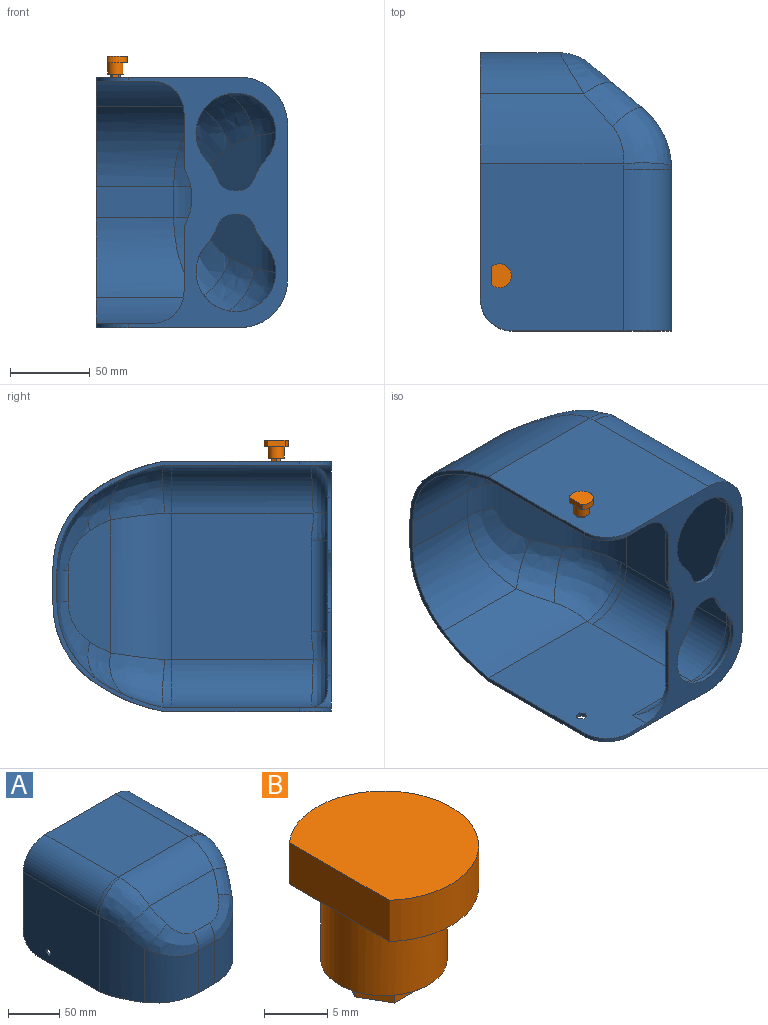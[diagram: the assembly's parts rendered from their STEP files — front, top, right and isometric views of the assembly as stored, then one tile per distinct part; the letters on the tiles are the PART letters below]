
ASSEMBLY  parts=2 mates=1
PART A: 87 faces, bbox 158.6x174.5x120.3 mm
  f0: cylinder r=110.63mm len=87.5mm, axis (0,0,-1), area 3450.1mm2, adj f5,f10,f17,f57,f58,f59
  f1: cylinder r=110.63mm len=87.5mm, axis (0,0,-1), area 3450.1mm2, adj f6,f9,f17,f64,f65,f66
  f2: plane 83.39x31.77mm, normal (0,0.77,-0.64), area 2722mm2, adj f54,f59,f60,f61,f62,f64
  f3: plane 157x100mm, normal (0,1,0), area 5587mm2, adj f4,f5,f6,f11,f15,f16,f21,f23
  f4: plane 33.64x2.5mm, normal (0,0,-1), area 84.1mm2, adj f3,f22,f25,f26
  f5: plane 104.74x87.5mm, normal (1,0,0), area 8392.5mm2, adj f0,f3,f17,f24,f40,f48,f49,f50
  f6: plane 104.74x87.5mm, normal (-1,0,0), area 8392.5mm2, adj f1,f3,f17,f25,f41,f42,f43,f44
  f7: plane 92.01x88.86mm, normal (0,0,-1), area 8078.7mm2, adj f54,f56,f63,f81,f82,f83
  f8: plane 48.58x19.33mm, normal (0,1,0), area 939.2mm2, adj f9,f10,f17,f61
  f9: cylinder r=60mm len=64.79mm, axis (0,0,-1), area 3375.4mm2, adj f1,f8,f17,f62
  f10: cylinder r=60mm len=64.79mm, axis (0,0,-1), area 3375.4mm2, adj f0,f8,f17,f60
  f11: plane 104.97x90mm, normal (-1,0,0), area 9330mm2, adj f3,f12,f17,f40,f48,f49,f50,f51
  f12: cylinder r=113.13mm len=90mm, axis (0,0,-1), area 3852.8mm2, adj f11,f17,f19,f68,f69,f70
  f13: plane 49.49x22mm, normal (0,-1,0), area 1088.6mm2, adj f17,f18,f19,f72
  f14: cylinder r=113.13mm len=90mm, axis (0,0,-1), area 3852.8mm2, adj f15,f17,f18,f75,f76,f77
  f15: plane 104.97x90mm, normal (1,0,0), area 9330mm2, adj f3,f14,f17,f41,f42,f43,f44,f45
  f16: plane 101.18x97mm, normal (0,0,1), area 9814.9mm2, adj f3,f55,f67,f73
  f17: plane 157x154.5mm, normal (0,0,-1), area 1023.4mm2, adj f0,f1,f5,f6,f8,f9,f10,f11
  f18: cylinder r=60mm len=64.94mm, axis (0,0,-1), area 3318.7mm2, adj f13,f14,f17,f74
  f19: cylinder r=60mm len=64.94mm, axis (0,0,-1), area 3318.7mm2, adj f12,f13,f17,f71
  f20: plane 87.84x33.36mm, normal (0,-0.77,0.64), area 3020.2mm2, adj f55,f70,f71,f72,f74,f76
  f21: plane 39.64x2.5mm, normal (0,0,-1), area 99.1mm2, adj f3,f22,f24,f27
  f22: plane 132x55.18mm, normal (0,-1,0), area 2589.6mm2, adj f4,f21,f23,f24,f25,f26,f27,f28
  f23: cylinder r=35mm len=33.89mm, axis (0,1,0), area 88.4mm2, adj f3,f22,f26,f27
  f24: cylinder r=20mm len=20mm, axis (0,-1,0), area 157.9mm2, adj f3,f5,f21,f22,f78
  f25: cylinder r=20mm len=20mm, axis (0,1,0), area 157.9mm2, adj f3,f4,f6,f22,f85
  f26: cylinder r=5mm len=2.5mm, axis (0,1,0), area 6.3mm2, adj f3,f4,f22,f23
  f27: cylinder r=5mm len=2.5mm, axis (0,1,0), area 6.3mm2, adj f3,f21,f22,f23
  f28: cylinder r=25mm len=50mm, axis (0,1,0), area 278.5mm2, adj f3,f22,f29,f33,f79,f80,f81
  f29: cylinder r=41.31mm len=14.09mm, axis (0,1,0), area 41.6mm2, adj f3,f22,f28,f30
  f30: cylinder r=10mm len=9.4mm, axis (0,1,0), area 30.6mm2, adj f3,f22,f29,f31
  f31: plane 3.54x2.5mm, normal (-1,0,0), area 8.8mm2, adj f3,f22,f30,f32
  f32: cylinder r=10mm len=9.4mm, axis (0,1,0), area 30.6mm2, adj f3,f22,f31,f33
  f33: cylinder r=41.31mm len=14.09mm, axis (0,1,0), area 41.6mm2, adj f3,f22,f28,f32
  f34: cylinder r=10mm len=9.4mm, axis (0,1,0), area 30.6mm2, adj f3,f22,f35,f39
  f35: cylinder r=41.31mm len=13.04mm, axis (0,1,0), area 38.1mm2, adj f3,f22,f34,f36
  f36: cylinder r=25mm len=50mm, axis (0,1,0), area 285.9mm2, adj f3,f22,f35,f37,f83,f84,f86
  f37: cylinder r=41.31mm len=13.04mm, axis (0,1,0), area 38.1mm2, adj f3,f22,f36,f38
  f38: cylinder r=10mm len=9.4mm, axis (0,1,0), area 30.6mm2, adj f3,f22,f37,f39
  f39: plane 3.54x2.5mm, normal (1,0,0), area 8.8mm2, adj f3,f22,f34,f38
  f40: cylinder r=20mm len=20mm, axis (-1,0,0), area 78.5mm2, adj f3,f5,f11,f17
  f41: cylinder r=20mm len=20mm, axis (1,0,0), area 78.5mm2, adj f3,f6,f15,f17
  f42: plane 3x2.5mm, normal (0,0.5,0.87), area 8.7mm2, adj f6,f15,f43,f47
  f43: plane 3.46x2.5mm, normal (0,1,0), area 8.7mm2, adj f6,f15,f42,f44
  f44: plane 3x2.5mm, normal (0,0.5,-0.87), area 8.7mm2, adj f6,f15,f43,f45
  f45: plane 3x2.5mm, normal (0,-0.5,-0.87), area 8.7mm2, adj f6,f15,f44,f46
  f46: plane 3.46x2.5mm, normal (0,-1,0), area 8.7mm2, adj f6,f15,f45,f47
  f47: plane 3x2.5mm, normal (0,-0.5,0.87), area 8.7mm2, adj f6,f15,f42,f46
  f48: plane 3x2.5mm, normal (0,-0.5,0.87), area 8.7mm2, adj f5,f11,f49,f53
  f49: plane 3.46x2.5mm, normal (0,-1,0), area 8.7mm2, adj f5,f11,f48,f50
  f50: plane 3x2.5mm, normal (0,-0.5,-0.87), area 8.7mm2, adj f5,f11,f49,f51
  f51: plane 3x2.5mm, normal (0,0.5,-0.87), area 8.7mm2, adj f5,f11,f50,f52
  f52: plane 3.46x2.5mm, normal (0,1,0), area 8.7mm2, adj f5,f11,f51,f53
  f53: plane 3x2.5mm, normal (0,0.5,0.87), area 8.7mm2, adj f5,f11,f48,f52
  f54: cylinder r=50mm len=92mm, axis (1,0,0), area 3844.8mm2, adj f2,f7,f57,f58,f65,f66
  f55: cylinder r=50mm len=97mm, axis (1,0,0), area 4041.8mm2, adj f16,f20,f68,f69,f75,f77
  f56: cylinder r=30mm len=88.77mm, axis (0,-1,0), area 4161.2mm2, adj f5,f7,f57,f80
  f57: torus R=20mm, axis (-1,0,0), area 251.9mm2, adj f0,f5,f54,f56,f58
  f58: bspline ~51.33x39.96mm, area 1529.2mm2, adj f0,f54,f57,f59
  f59: bspline ~39.58x37.07mm, area 854.9mm2, adj f0,f2,f58,f60
  f60: bspline ~53.27x38.51mm, area 1263.7mm2, adj f2,f10,f59,f61
  f61: cylinder r=30mm len=19.33mm, axis (1,0,0), area 404.9mm2, adj f2,f8,f60,f62
  f62: bspline ~53.27x38.51mm, area 1263.7mm2, adj f2,f9,f61,f64
  f63: cylinder r=30mm len=88.77mm, axis (0,1,0), area 4161.2mm2, adj f6,f7,f65,f84
  f64: bspline ~39.58x37.07mm, area 854.9mm2, adj f1,f2,f62,f66
  f65: torus R=20mm, axis (-1,0,0), area 251.9mm2, adj f1,f6,f54,f63,f66
  f66: bspline ~51.33x39.96mm, area 1529.2mm2, adj f1,f54,f64,f65
  f67: cylinder r=30mm len=101.18mm, axis (0,1,0), area 4768.2mm2, adj f3,f11,f16,f68
  f68: torus R=20mm, axis (-1,0,0), area 168.1mm2, adj f11,f12,f55,f67,f69
  f69: bspline ~51.33x39.92mm, area 1615mm2, adj f12,f55,f68,f70
  f70: bspline ~45.39x40.62mm, area 977.5mm2, adj f12,f20,f69,f71
  f71: bspline ~53.27x38.51mm, area 1216.6mm2, adj f19,f20,f70,f72
  f72: cylinder r=30mm len=22mm, axis (-1,0,0), area 460.7mm2, adj f13,f20,f71,f74
  f73: cylinder r=30mm len=101.18mm, axis (0,-1,0), area 4768.2mm2, adj f3,f15,f16,f75
  f74: bspline ~53.27x38.51mm, area 1216.6mm2, adj f18,f20,f72,f76
  f75: torus R=20mm, axis (-1,0,0), area 168.1mm2, adj f14,f15,f55,f73,f77
  f76: bspline ~45.39x40.62mm, area 977.5mm2, adj f14,f20,f74,f77
  f77: bspline ~51.33x39.92mm, area 1615mm2, adj f14,f55,f75,f76
  f78: cylinder r=10mm len=41.6mm, axis (0,0,1), area 517.5mm2, adj f5,f22,f24,f79
  f79: bspline ~14.27x10.62mm, area 152.7mm2, adj f5,f28,f78,f80
  f80: bspline ~34.3x31.74mm, area 530.2mm2, adj f28,f56,f79,f81
  f81: bspline ~23.68x11.42mm, area 213.6mm2, adj f7,f28,f80,f82
  f82: cylinder r=10mm len=57mm, axis (1,0,0), area 895.4mm2, adj f7,f22,f81,f83
  f83: bspline ~23.68x11.42mm, area 213.6mm2, adj f7,f36,f82,f84
  f84: bspline ~30x30mm, area 530.2mm2, adj f36,f63,f83,f86
  f85: cylinder r=10mm len=41.6mm, axis (0,0,-1), area 517.5mm2, adj f6,f22,f25,f86
  f86: bspline ~14.27x10.62mm, area 152.7mm2, adj f6,f36,f84,f85
PART B: 16 faces, bbox 12.5x15x13 mm
  f0: cylinder r=7.5mm len=15mm, axis (0,0,-1), area 138mm2, adj f1,f2,f12
  f1: plane 15x12.5mm, normal (0,0,1), area 157.4mm2, adj f0,f12
  f2: plane 15x12.5mm, normal (0,0,-1), area 78.8mm2, adj f0,f11,f12
  f3: plane 2.85x2mm, normal (0.87,0.5,0), area 6.6mm2, adj f4,f8,f9,f10
  f4: plane 3.29x2mm, normal (0,1,0), area 6.6mm2, adj f3,f5,f9,f10
  f5: plane 2.85x2mm, normal (-0.87,0.5,0), area 6.6mm2, adj f4,f6,f9,f10
  f6: plane 2.85x2mm, normal (-0.87,-0.5,0), area 6.6mm2, adj f5,f7,f9,f10
  f7: plane 3.29x2mm, normal (0,-1,0), area 6.6mm2, adj f6,f8,f9,f10
  f8: plane 2.85x2mm, normal (0.87,-0.5,0), area 6.6mm2, adj f3,f7,f9,f10
  f9: plane 6.58x5.7mm, normal (0,0,-1), area 19.6mm2, adj f3,f4,f5,f6,f7,f8,f15
  f10: plane 10x10mm, normal (0,0,-1), area 50.4mm2, adj f3,f4,f5,f6,f7,f8,f11
  f11: cylinder r=5mm len=10mm, axis (0,0,-1), area 219.9mm2, adj f2,f10
  f12: plane 11.18x4mm, normal (-1,0,0), area 44.7mm2, adj f0,f1,f2
  f13: cylinder r=1.4mm len=7.75mm, axis (0,0,-1), area 68.2mm2, adj f14,f15
  f14: plane 2.8x2.8mm, normal (0,0,-1), area 6.2mm2, adj f13
  f15: cone r=1.4mm half-angle=45deg, axis (0,0,-1), area 3.4mm2, adj f9,f13
PLACE A rot(axis=(0.71,0,0.71),180deg) t=(135.76,246.56,18.04)mm
PLACE B t=(147.76,91.06,20.54)mm
MATE revolute A.f15 <-> B.f13  axis (0,0,1) through (147.76,91.06,20.54)mm
